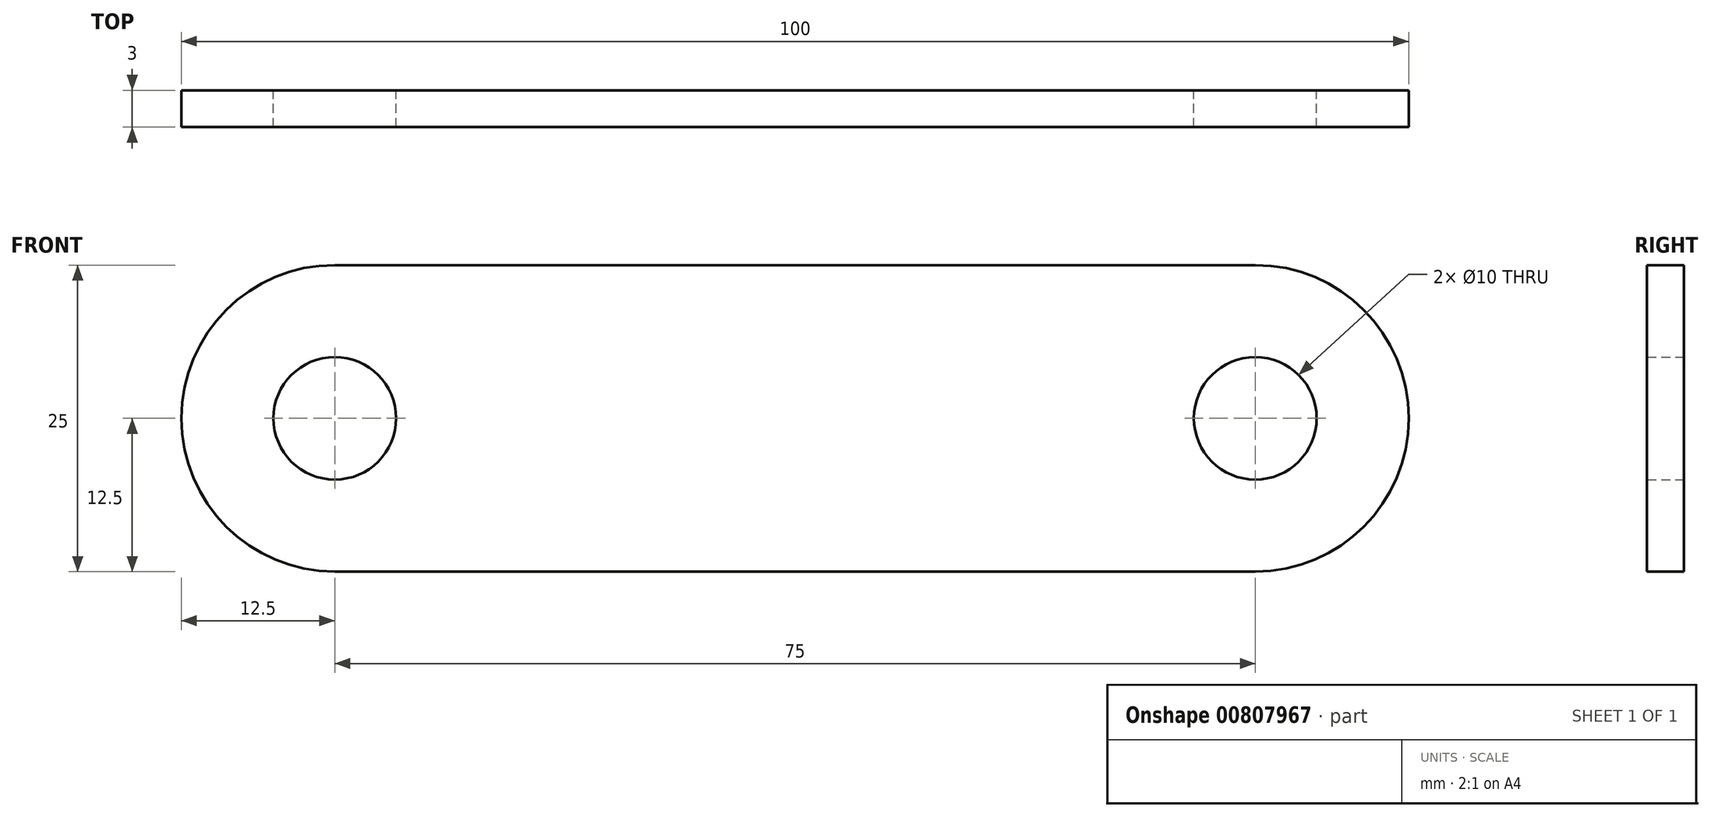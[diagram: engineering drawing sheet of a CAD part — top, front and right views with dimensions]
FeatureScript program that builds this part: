
annotation { "Feature Type Name" : "Feature", "Feature Type Description" : "" }
export const myFeature = defineFeature(function(context is Context, id is Id, definition is map)
    precondition{}
    {
        {
            var Q0;
            Q0=qCreatedBy(makeId("Front.planeOp"),FACE);
            var sketch = newSketch(context, id + "F0", { "sketchPlane" : qUnion([Q0])});
            skLineSegment(sketch, "E0.bottom", {"start": v(0, 0) * mm, "end": v(75, 0) * mm});
            skLineSegment(sketch, "E0.top", {"start": v(0, 25) * mm, "end": v(75, 25) * mm});
            skArc(sketch, "E1", {"start": v(0, 25) * mm, "mid": v(-12.5, 12.5) * mm, "end": v(0, 0) * mm});
            skPoint(sketch, "E1.third.point", {"position": v(-12.5, 12.5) * mm});
            skPoint(sketch, "E1.third.point.positionSnap0", {"position": v(0, 12.5) * mm});
            skArc(sketch, "E2", {"start": v(75, 0) * mm, "mid": v(87.5, 12.5) * mm, "end": v(75, 25) * mm});
            skPoint(sketch, "E2.third.point", {"position": v(86.14, 6.84) * mm});
            skCircle(sketch, "E3", {"center": v(75, 12.5) * mm, "radius": 5 * mm});
            skCircle(sketch, "E4", {"center": v(0, 12.5) * mm, "radius": 5 * mm});
            skSolve(sketch);
        }
        {
            var Q0;
            Q0=makeQuery(id+"F0.imprint","IMPRINT",FACE,{"disambiguationData":[TD([[makeQuery(id+"F0.imprint","IMPRINT",EDGE,{"derivedFrom":sQuery(id+"F0.wireOp",EDGE,"E0.bottom")}),1.0]])]});
            extrude(context, id + "F1", {"entities" : qUnion([Q0]), "depth" : 3 * mm, "offsetDistance" : 25 * mm});
        }
    });
